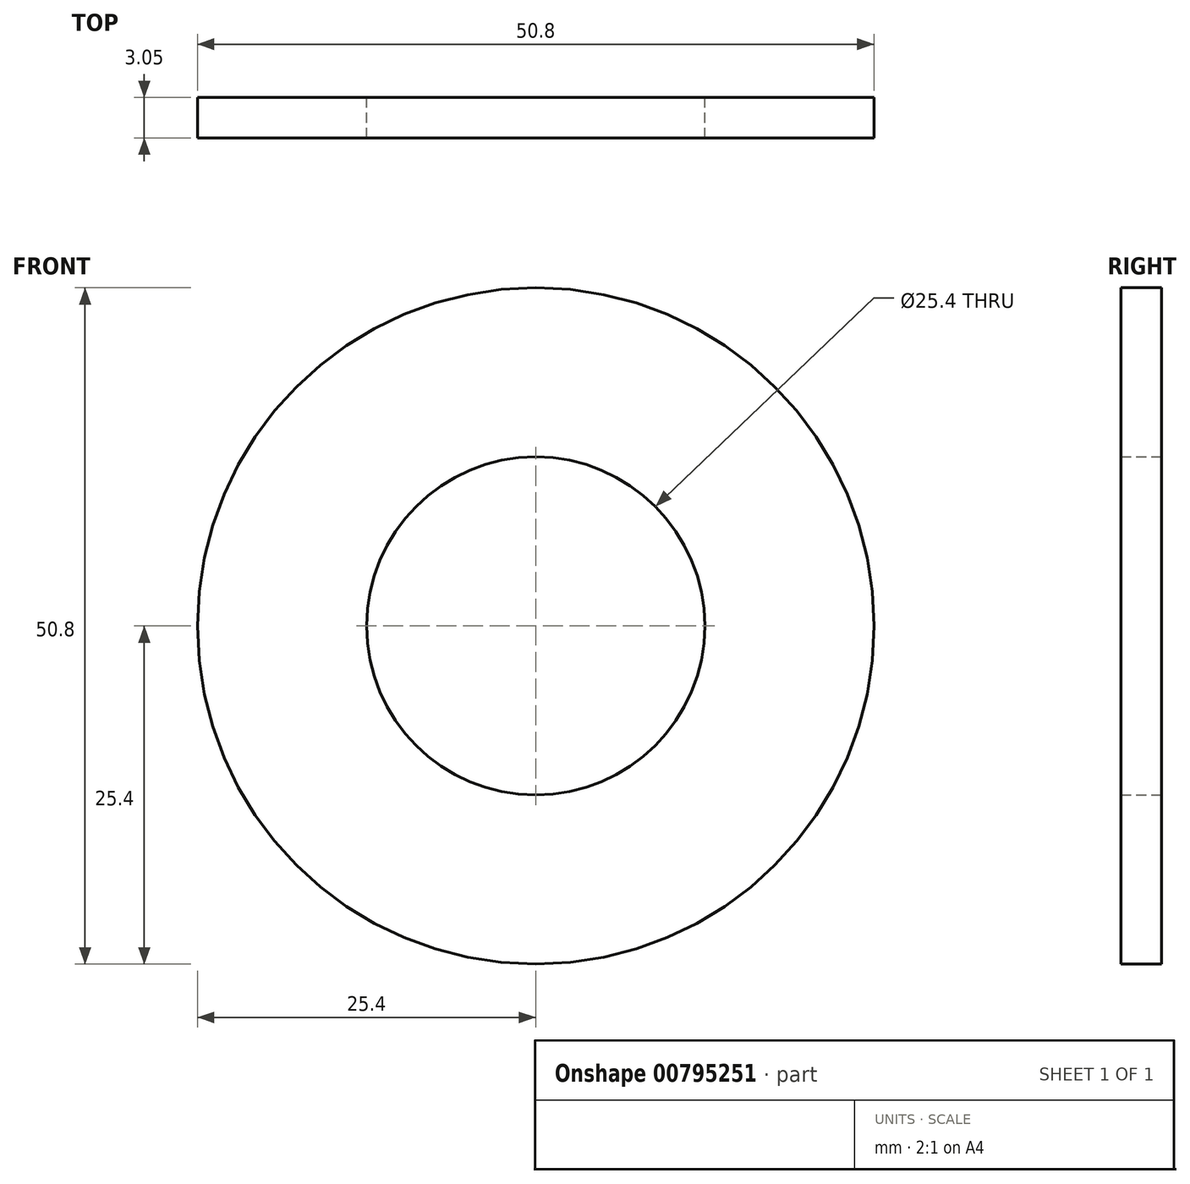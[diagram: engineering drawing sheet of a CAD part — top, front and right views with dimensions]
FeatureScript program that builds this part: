
annotation { "Feature Type Name" : "Feature", "Feature Type Description" : "" }
export const myFeature = defineFeature(function(context is Context, id is Id, definition is map)
    precondition{}
    {
        {
            var Q0;
            Q0=qCreatedBy(makeId("Front.planeOp"),FACE);
            var sketch = newSketch(context, id + "F0", { "sketchPlane" : qUnion([Q0])});
            skCircle(sketch, "E0", {"center": v(0, 0) * mm, "radius": 25.4 * mm});
            skCircle(sketch, "E1", {"center": v(0, 0) * mm, "radius": 12.7 * mm});
            skSolve(sketch);
        }
        {
            var Q0;
            Q0 = qSketchRegion(id + "F0", true);
            extrude(context, id + "F1", {"entities" : qUnion([Q0]), "depth" : 3.05 * mm, "offsetDistance" : 25.4 * mm});
        }
    });
